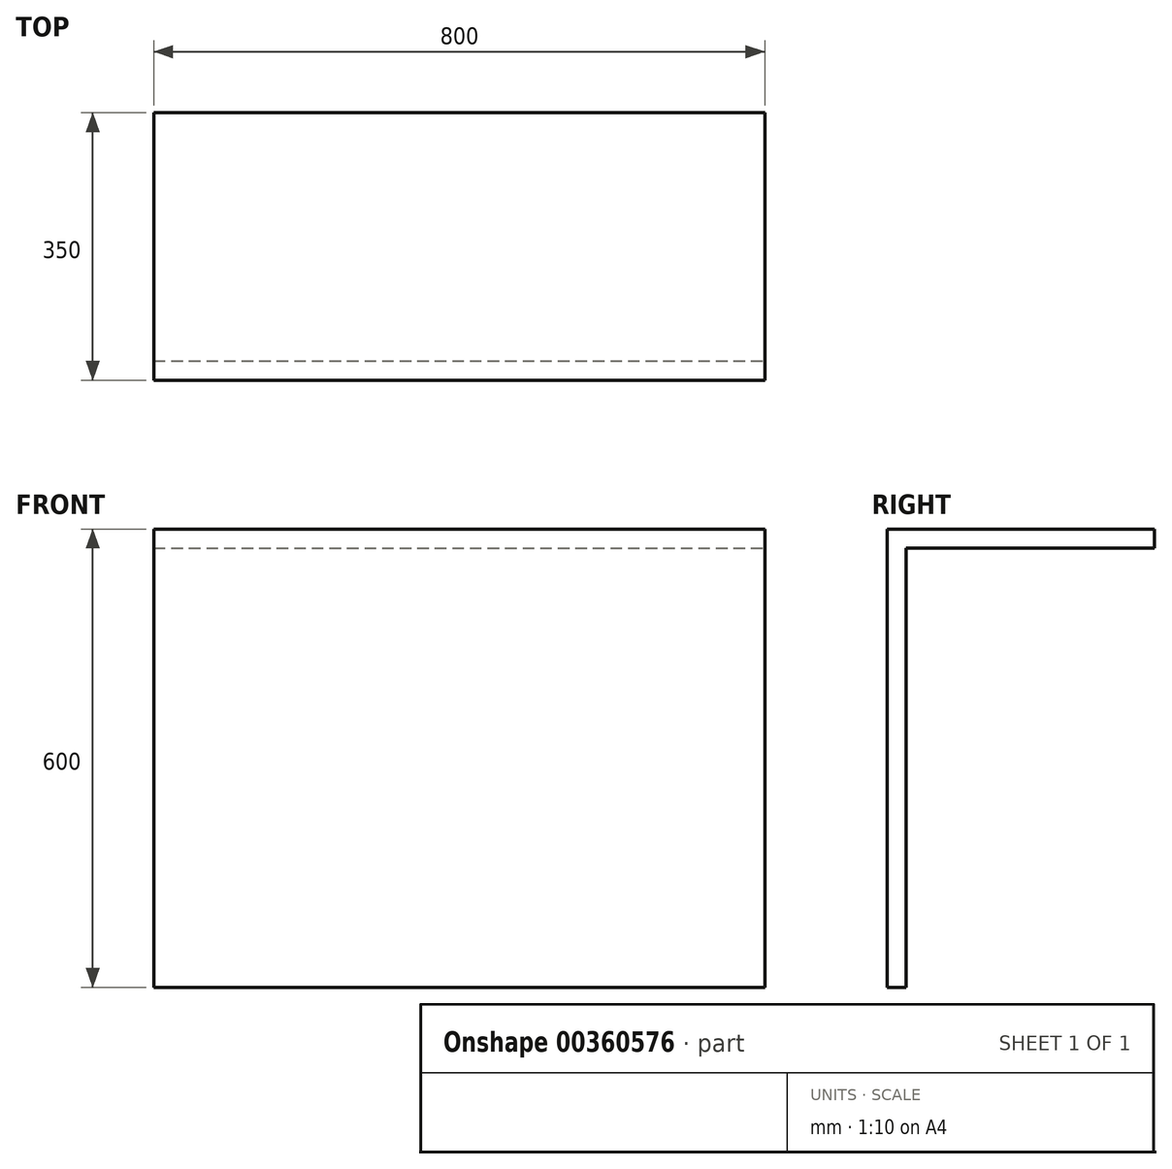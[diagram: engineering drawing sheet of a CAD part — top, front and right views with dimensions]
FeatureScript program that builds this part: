
annotation { "Feature Type Name" : "Feature", "Feature Type Description" : "" }
export const myFeature = defineFeature(function(context is Context, id is Id, definition is map)
    precondition{}
    {
        {
            var Q0;
            Q0=qCreatedBy(makeId("Right.planeOp"),FACE);
            var sketch = newSketch(context, id + "F0", { "sketchPlane" : qUnion([Q0])});
            skLineSegment(sketch, "E0", {"start": v(0, 0) * mm, "end": v(0, 600) * mm});
            skLineSegment(sketch, "E1", {"start": v(0, 600) * mm, "end": v(350, 600) * mm});
            skLineSegment(sketch, "E2", {"start": v(350, 600) * mm, "end": v(350, 575) * mm});
            skLineSegment(sketch, "E3", {"start": v(350, 575) * mm, "end": v(25, 575) * mm});
            skLineSegment(sketch, "E4", {"start": v(25, 575) * mm, "end": v(25, 0) * mm});
            skLineSegment(sketch, "E5", {"start": v(25, 0) * mm, "end": v(0, 0) * mm});
            skSolve(sketch);
        }
        {
            var Q0;
            Q0 = qSketchRegion(id + "F0", true);
            extrude(context, id + "F1", {"entities" : qUnion([Q0]), "oppositeDirection" : true, "depth" : 800 * mm});
        }
    });
